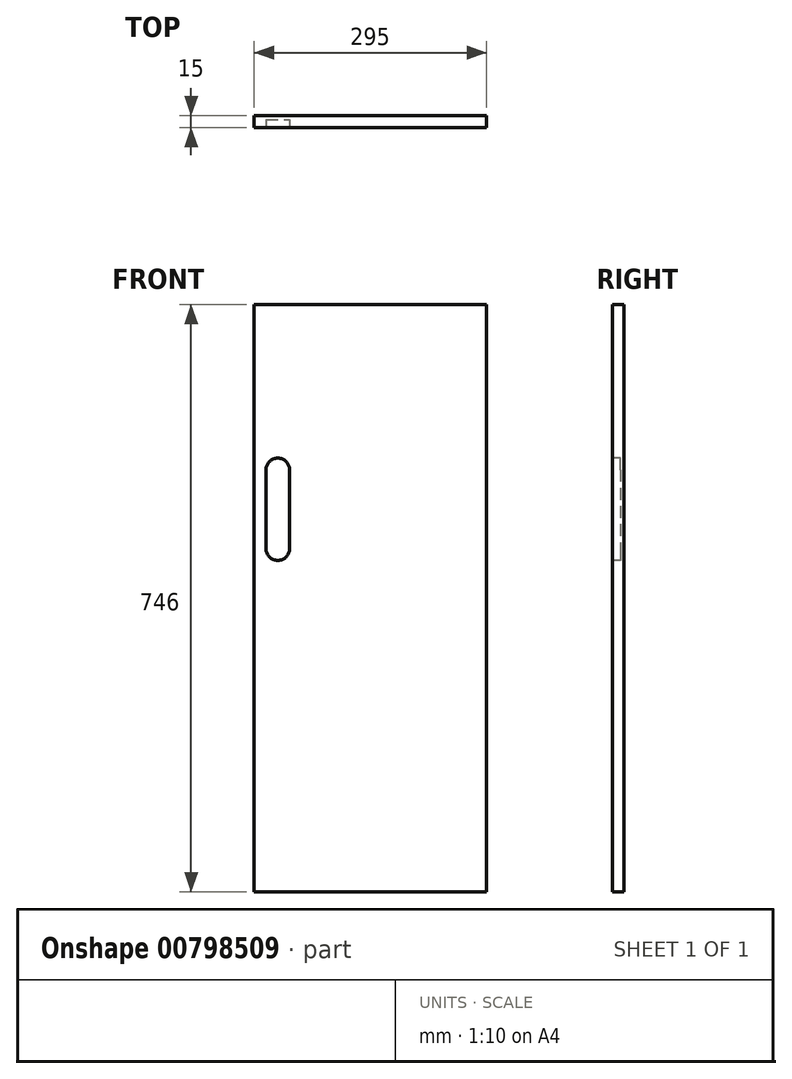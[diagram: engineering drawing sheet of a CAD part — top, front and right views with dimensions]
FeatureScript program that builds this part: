
annotation { "Feature Type Name" : "Feature", "Feature Type Description" : "" }
export const myFeature = defineFeature(function(context is Context, id is Id, definition is map)
    precondition{}
    {
        {
            var Q0;
            Q0=qCreatedBy(makeId("Front.planeOp"),FACE);
            var sketch = newSketch(context, id + "F0", { "sketchPlane" : qUnion([Q0])});
            skLineSegment(sketch, "E0.bottom", {"start": v(0, 0) * mm, "end": v(295, 0) * mm});
            skLineSegment(sketch, "E0.top", {"start": v(0, -746) * mm, "end": v(295, -746) * mm});
            skLineSegment(sketch, "E0.left", {"start": v(0, 0) * mm, "end": v(0, -746) * mm});
            skLineSegment(sketch, "E0.right", {"start": v(295, 0) * mm, "end": v(295, -746) * mm});
            skSolve(sketch);
        }
        {
            var Q0;
            Q0=makeQuery(id+"F0.imprint","IMPRINT",FACE,{"disambiguationData":[TD([[makeQuery(id+"F0.imprint","IMPRINT",EDGE,{"derivedFrom":sQuery(id+"F0.wireOp",EDGE,"E0.bottom")}),-1.0]])]});
            extrude(context, id + "F1", {"entities" : qUnion([Q0]), "depth" : 15 * mm, "offsetDistance" : 25 * mm});
        }
        {
            var Q0;
            Q0=makeQuery(id+"F1.opExtrude","CAP_FACE",FACE,{"disambiguationData":[OSD([sQuery(id+"F0.wireOp",EDGE,"E0.bottom"),sQuery(id+"F0.wireOp",EDGE,"E0.top"),sQuery(id+"F0.wireOp",EDGE,"E0.left"),sQuery(id+"F0.wireOp",EDGE,"E0.right")])],"isStart":false});
            var sketch = newSketch(context, id + "F2", { "sketchPlane" : qUnion([Q0])});
            skCircle(sketch, "E1", {"center": v(30, -210) * mm, "radius": 15 * mm});
            skCircle(sketch, "E2", {"center": v(30, -310) * mm, "radius": 15 * mm});
            skLineSegment(sketch, "E3", {"start": v(45, -210) * mm, "end": v(45, -310) * mm});
            skLineSegment(sketch, "E4", {"start": v(15, -210) * mm, "end": v(15, -310) * mm});
            skSolve(sketch);
        }
        {
            var Q0;
            {var subQ0=sQuery(id+"F2.wireOp",EDGE,"E2");var subQ1=makeQuery(id+"F2.imprint","INTERSECT",VERTEX,{"derivedFrom":[subQ0,sQuery(id+"F2.wireOp",EDGE,"E3")]});Q0=makeQuery(id+"F2.imprint","IMPRINT",FACE,{"disambiguationData":[TD([[makeQuery(id+"F2.imprint","IMPRINT",EDGE,{"disambiguationData":[TD([[subQ1,-1.0]])],"derivedFrom":subQ0}),1.0]])]});}
            var Q1;
            {var subQ0=sQuery(id+"F2.wireOp",EDGE,"E3");Q1=makeQuery(id+"F2.imprint","IMPRINT",FACE,{"disambiguationData":[TD([[makeQuery(id+"F2.imprint","IMPRINT",EDGE,{"derivedFrom":subQ0}),-1.0]])]});}
            var Q2;
            {var subQ0=sQuery(id+"F2.wireOp",EDGE,"E1");var subQ1=makeQuery(id+"F2.imprint","INTERSECT",VERTEX,{"derivedFrom":[subQ0,sQuery(id+"F2.wireOp",EDGE,"E3")]});Q2=makeQuery(id+"F2.imprint","IMPRINT",FACE,{"disambiguationData":[TD([[makeQuery(id+"F2.imprint","IMPRINT",EDGE,{"disambiguationData":[TD([[subQ1,-1.0]])],"derivedFrom":subQ0}),1.0]])]});}
            extrude(context, id + "F3", {"entities" : qUnion([Q0, Q1, Q2]), "operationType" : NewBodyOperationType.REMOVE, "oppositeDirection" : true, "depth" : 10 * mm, "offsetDistance" : 25 * mm});
        }
    });
